AUTODESK INVENTOR PART (.ipt)
format: ipt  version: 2021 (Build 250183000, 183)  size: 116,736 bytes
history: native  units: mm
features: extrude x2, sketch x2, fillet x1
ambient origin geometry x8: Origin, YZ Plane, XZ Plane, XY Plane, X Axis, Y Axis, Z Axis, Center Point
bodies: Solid1 (feature_tree)
feature tree (5):
  extrude  "Extrusion1"  Depth=5.4mm
  extrude  "Extrusion2"  Depth=5.4mm
  fillet  "Fillet1"  Radius=5.4mm
  sketch  "Sketch1"  dims[d0=5.4mm d1=3.0mm]
  sketch  "Sketch2"  dims[d2=2.4mm d3=0.0mm d4=5.4mm d5=5.4mm d6=1.4mm d7=0.0mm d8=0.4mm]
